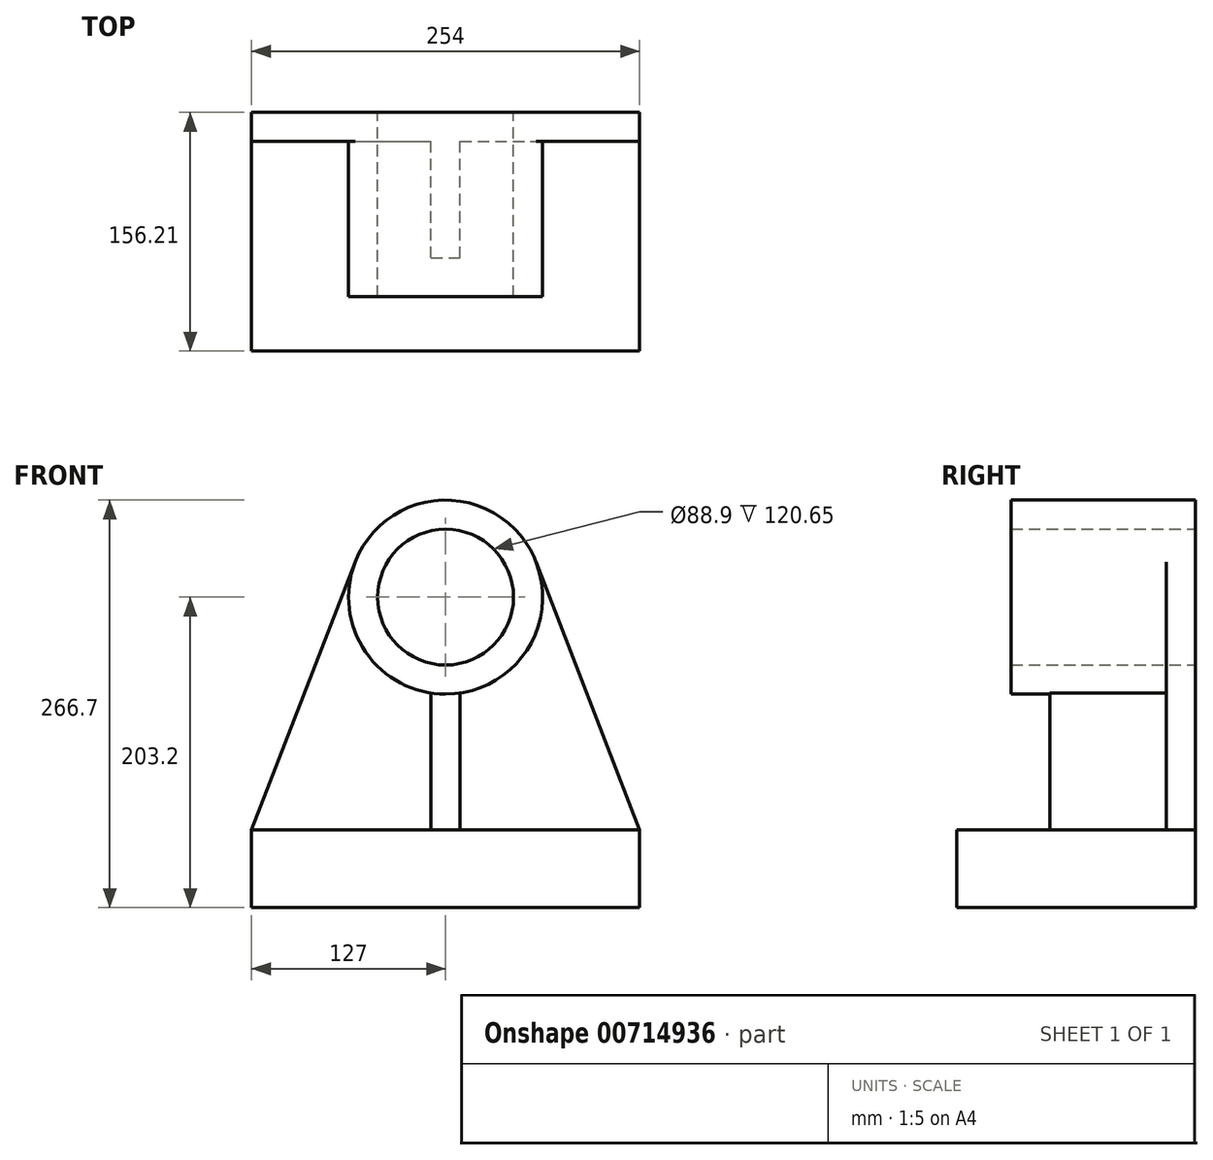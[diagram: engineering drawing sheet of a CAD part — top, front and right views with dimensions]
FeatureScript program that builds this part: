
annotation { "Feature Type Name" : "Feature", "Feature Type Description" : "" }
export const myFeature = defineFeature(function(context is Context, id is Id, definition is map)
    precondition{}
    {
        {
            var Q0;
            Q0=qCreatedBy(makeId("Front.planeOp"),FACE);
            var sketch = newSketch(context, id + "F0", { "sketchPlane" : qUnion([Q0])});
            skCircle(sketch, "E0", {"center": v(0, 0) * mm, "radius": 63.5 * mm});
            skLineSegment(sketch, "E1", {"start": v(127, -152.4) * mm, "end": v(127, -203.2) * mm});
            skLineSegment(sketch, "E2", {"start": v(127, -203.2) * mm, "end": v(-127, -203.2) * mm});
            skLineSegment(sketch, "E3", {"start": v(-127, -203.2) * mm, "end": v(-127, -152.4) * mm});
            skCircle(sketch, "E4", {"center": v(0, 0) * mm, "radius": 44.45 * mm});
            skLineSegment(sketch, "E5", {"start": v(-127, -152.4) * mm, "end": v(-59.23, 22.9) * mm});
            skLineSegment(sketch, "E6", {"start": v(127, -152.4) * mm, "end": v(59.23, 22.9) * mm});
            skSolve(sketch);
        }
        {
            var Q0;
            Q0 = qSketchRegion(id + "F0", true);
            extrude(context, id + "F1", {"entities" : qUnion([Q0]), "depth" : 19.05 * mm, "offsetDistance" : 25.4 * mm});
        }
        {
            var Q0;
            Q0=makeQuery(id+"F1.opExtrude","CAP_FACE",FACE,{"disambiguationData":[OSD([sQuery(id+"F0.wireOp",EDGE,"E0"),sQuery(id+"F0.wireOp",EDGE,"E1"),sQuery(id+"F0.wireOp",EDGE,"E2"),sQuery(id+"F0.wireOp",EDGE,"E3"),sQuery(id+"F0.wireOp",EDGE,"E4"),sQuery(id+"F0.wireOp",EDGE,"E5"),sQuery(id+"F0.wireOp",EDGE,"E6")])],"isStart":false});
            var sketch = newSketch(context, id + "F2", { "sketchPlane" : qUnion([Q0])});
            skLineSegment(sketch, "E7", {"start": v(-127, -203.2) * mm, "end": v(-127, -152.4) * mm});
            skLineSegment(sketch, "E8", {"start": v(-127, -152.4) * mm, "end": v(127, -152.4) * mm});
            skLineSegment(sketch, "E9", {"start": v(127, -152.4) * mm, "end": v(127, -203.2) * mm});
            skLineSegment(sketch, "E10", {"start": v(127, -203.2) * mm, "end": v(-127, -203.2) * mm});
            skSolve(sketch);
        }
        {
            var Q0;
            Q0 = qSketchRegion(id + "F2", true);
            extrude(context, id + "F3", {"entities" : qUnion([Q0]), "operationType" : NewBodyOperationType.ADD, "depth" : 137.16 * mm, "offsetDistance" : 25.4 * mm});
        }
        {
            var Q0;
            Q0=makeQuery(id+"F1.opExtrude","CAP_FACE",FACE,{"disambiguationData":[OSD([sQuery(id+"F0.wireOp",EDGE,"E0"),sQuery(id+"F0.wireOp",EDGE,"E1"),sQuery(id+"F0.wireOp",EDGE,"E2"),sQuery(id+"F0.wireOp",EDGE,"E3"),sQuery(id+"F0.wireOp",EDGE,"E4"),sQuery(id+"F0.wireOp",EDGE,"E5"),sQuery(id+"F0.wireOp",EDGE,"E6")])],"isStart":false});
            var sketch = newSketch(context, id + "F4", { "sketchPlane" : qUnion([Q0])});
            skCircle(sketch, "E11", {"center": v(0, 0) * mm, "radius": 44.45 * mm});
            skCircle(sketch, "E12", {"center": v(0, 0) * mm, "radius": 63.5 * mm});
            skSolve(sketch);
        }
        {
            var Q0;
            Q0 = qSketchRegion(id + "F4", true);
            extrude(context, id + "F5", {"entities" : qUnion([Q0]), "operationType" : NewBodyOperationType.ADD, "depth" : 101.6 * mm, "offsetDistance" : 25.4 * mm});
        }
        {
            var Q0;
            Q0=makeQuery(id+"F1.opExtrude","CAP_FACE",FACE,{"disambiguationData":[OSD([sQuery(id+"F0.wireOp",EDGE,"E0"),sQuery(id+"F0.wireOp",EDGE,"E1"),sQuery(id+"F0.wireOp",EDGE,"E2"),sQuery(id+"F0.wireOp",EDGE,"E3"),sQuery(id+"F0.wireOp",EDGE,"E4"),sQuery(id+"F0.wireOp",EDGE,"E5"),sQuery(id+"F0.wireOp",EDGE,"E6")])],"isStart":false});
            var sketch = newSketch(context, id + "F6", { "sketchPlane" : qUnion([Q0])});
            skLineSegment(sketch, "E13", {"start": v(-9.53, -62.78) * mm, "end": v(-9.52, -152.4) * mm});
            skLineSegment(sketch, "E14", {"start": v(-9.52, -152.4) * mm, "end": v(9.53, -152.4) * mm});
            skLineSegment(sketch, "E15", {"start": v(9.52, -62.78) * mm, "end": v(-9.53, -62.78) * mm});
            skLineSegment(sketch, "E16", {"start": v(9.52, -62.78) * mm, "end": v(9.53, -152.4) * mm});
            skSolve(sketch);
        }
        {
            var Q0;
            Q0 = qSketchRegion(id + "F6", true);
            extrude(context, id + "F7", {"entities" : qUnion([Q0]), "operationType" : NewBodyOperationType.ADD, "depth" : 76.2 * mm, "offsetDistance" : 25.4 * mm});
        }
    });
